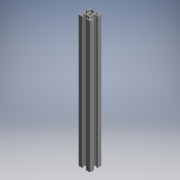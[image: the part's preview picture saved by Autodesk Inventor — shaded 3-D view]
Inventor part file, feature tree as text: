
AUTODESK INVENTOR PART (.ipt)
format: ipt  version: 2017.3 (Build 213256000, 256)  size: 208,384 bytes
history: native  units: mm (DEFAULTED — no unit token found)
features: other x7, sketch x2, extrude x1, hole x1
ambient origin geometry x8: Origin, YZ Plane, XZ Plane, XY Plane, X Axis, Y Axis, Z Axis, Center Point
bodies: Solid1 (feature_tree)
feature tree (11):
  extrude  "Extrusion1"  TaperAngle=0.0deg  [1 undecoded]
  hole  "Hole1"  [1 undecoded]
  other  "C1_XY"
  other  "C1_YZ"
  other  "C1_ZX"
  other  "C1_X"
  other  "C1_Y"
  other  "C1_Z"
  other  "C1_Center"
  sketch  "Sketch_75"  dims[d2=4.2mm d3=6.0mm d4=4.0mm d5=2.0mm d6=90.0deg d7=225.0mm d8=0.0mm d9=0.0mm]
  sketch  "Sketch2"  dims[d0=225.0mm d1=0.0mm]
note: 2 required parameter values undecoded (feature->parameter linkage not recoverable at this tier; creation-order binding heuristic only, values carry confidence <= 0.55)
